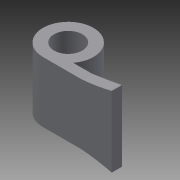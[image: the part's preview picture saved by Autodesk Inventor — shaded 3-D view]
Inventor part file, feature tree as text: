
AUTODESK INVENTOR PART (.ipt)
format: ipt  version: 2013 (Build 170138000, 138)  size: 139,776 bytes
history: native  units: in
note: dims shown in document units (in); Inventor stores cm internally (conversion verified against a paired STEP export)
features: sketch x6, plane x5, projected_geometry x4, extrude x2, loft x1
ambient origin geometry x8: Origin, YZ Plane, XZ Plane, XY Plane, X Axis, Y Axis, Z Axis, Center Point
bodies: Solid1 (feature_tree)
feature tree (18):
  extrude  "Extrusion1"  Depth=0.1969in
  plane  "Work Plane2"
  plane  "Work Plane7"
  sketch  "Sketch15"  dims[d13=0.1181in]
  plane  "Work Plane4"
  plane  "Work Plane5"
  sketch  "Sketch12"  dims[d3=0.2362in d4=0.0in d7=0.0472in]
  plane  "Work Plane6"
  sketch  "Sketch13"  dims[d10=0.2756in d11=45.0deg]
  sketch  "Sketch14"  dims[d12=0.1443in]
  loft  "Loft3"
  extrude  "Extrusion3"  TaperAngle=45.0deg  [1 undecoded]
  sketch  "Sketch1"  dims[d0=0.1102in d2=0.1969in]
  projected_geometry  "Projected Loop8"
  projected_geometry  "Projected Loop9"
  projected_geometry  "Projected Loop10"
  sketch  "Sketch16"  dims[d16=0.0in d22=0.2681in d31=0.0984in d36=0.0197in d37=0.7087in d38=0.1181in d39=0.2756in d40=0.2362in d41=0.0394in d52=0.15in d53=0.2681in d56=0.0in d57=90.0deg d58=0.0in d59=90.0deg d60=0.15in d61=0.0394in d63=0.0in d64=90.0deg d67=0.0in d68=90.0deg d69=0.15in d70=0.0in d71=0.0197in d72=0.0197in]
  projected_geometry  "Projected Loop11"
note: 1 required parameter value undecoded (feature->parameter linkage not recoverable at this tier; creation-order binding heuristic only, values carry confidence <= 0.55)
